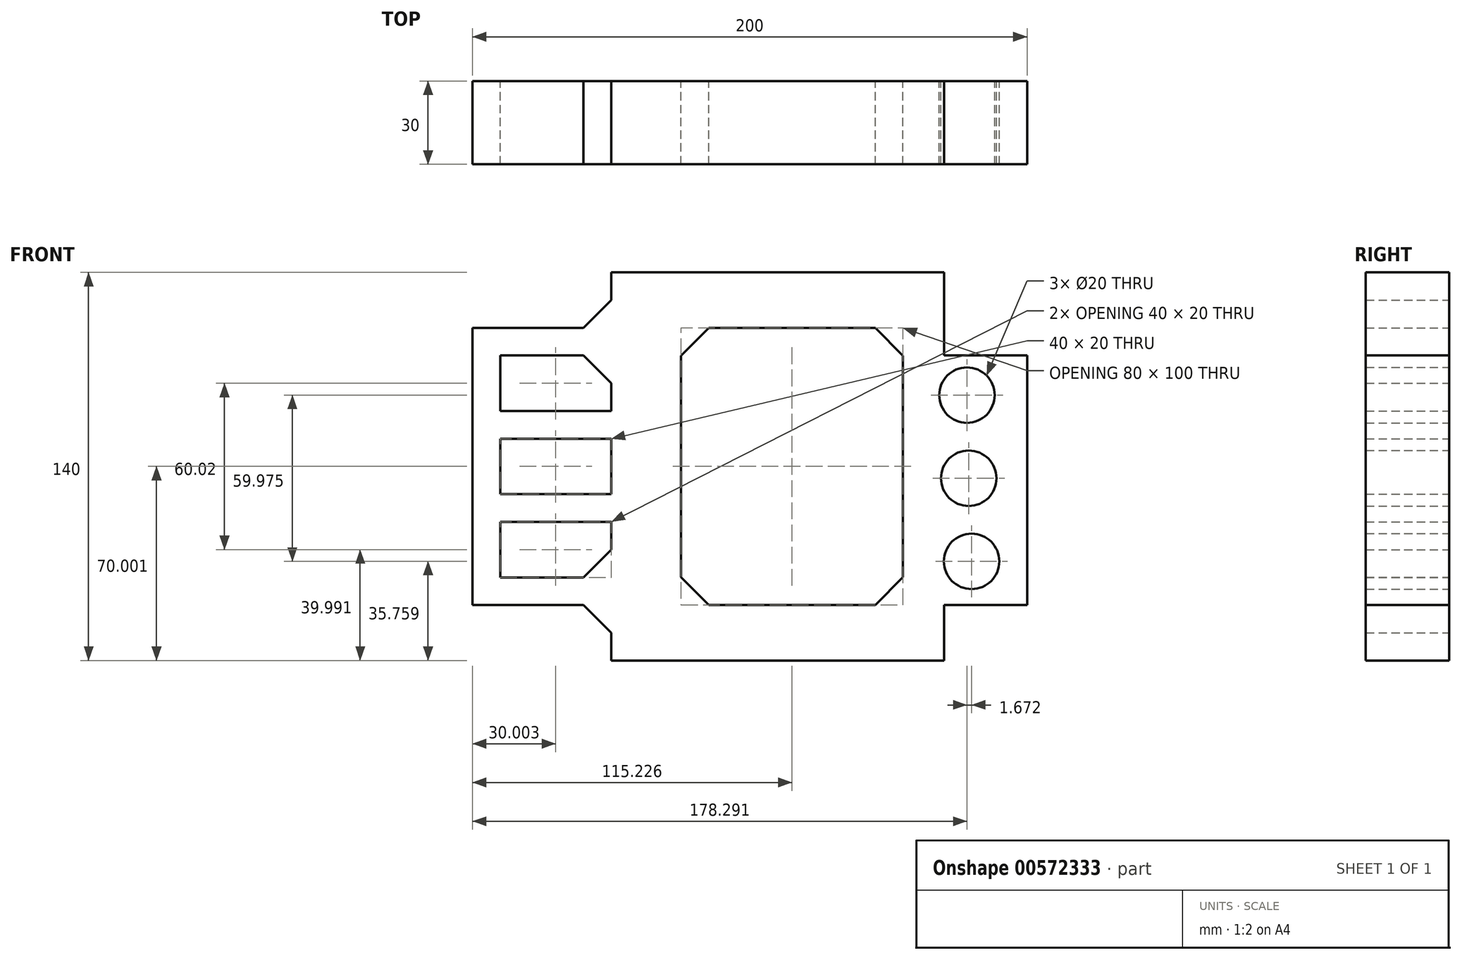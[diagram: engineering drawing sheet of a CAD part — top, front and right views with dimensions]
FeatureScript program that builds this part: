
annotation { "Feature Type Name" : "Feature", "Feature Type Description" : "" }
export const myFeature = defineFeature(function(context is Context, id is Id, definition is map)
    precondition{}
    {
        {
            var Q0;
            Q0=qCreatedBy(makeId("Front.planeOp"),FACE);
            var sketch = newSketch(context, id + "F0", { "sketchPlane" : qUnion([Q0])});
            skLineSegment(sketch, "E0", {"start": v(-36.99, 82.4) * mm, "end": v(63.01, 82.4) * mm});
            skLineSegment(sketch, "E1", {"start": v(73.01, 72.4) * mm, "end": v(73.01, 62.5) * mm});
            skLineSegment(sketch, "E2", {"start": v(83.01, 52.5) * mm, "end": v(93.01, 52.5) * mm});
            skLineSegment(sketch, "E3", {"start": v(103.01, 42.5) * mm, "end": v(103.01, -27.6) * mm});
            skLineSegment(sketch, "E4", {"start": v(93.01, -37.6) * mm, "end": v(83.01, -37.6) * mm});
            skLineSegment(sketch, "E5", {"start": v(73.01, -47.6) * mm, "end": v(73.01, -47.6) * mm});
            skLineSegment(sketch, "E6", {"start": v(63.01, -57.6) * mm, "end": v(-36.99, -57.6) * mm});
            skLineSegment(sketch, "E7", {"start": v(-46.99, -47.6) * mm, "end": v(-46.99, -47.6) * mm});
            skLineSegment(sketch, "E8", {"start": v(-56.99, -37.6) * mm, "end": v(-86.99, -37.6) * mm});
            skLineSegment(sketch, "E9", {"start": v(-96.99, -27.6) * mm, "end": v(-96.99, 52.4) * mm});
            skLineSegment(sketch, "E10", {"start": v(-86.99, 62.4) * mm, "end": v(-56.99, 62.4) * mm});
            skLineSegment(sketch, "E11", {"start": v(-46.99, 72.4) * mm, "end": v(-46.99, 72.4) * mm});
            skLineSegment(sketch, "E12", {"start": v(-11.76, 62.4) * mm, "end": v(48.24, 62.4) * mm});
            skLineSegment(sketch, "E13", {"start": v(58.24, 52.4) * mm, "end": v(58.24, 37.4) * mm});
            skLineSegment(sketch, "E14", {"start": v(48.24, -37.6) * mm, "end": v(-11.76, -37.6) * mm});
            skLineSegment(sketch, "E15", {"start": v(-21.76, -27.6) * mm, "end": v(-21.76, 12.4) * mm});
            skLineSegment(sketch, "E16.trimOffspring", {"start": v(-21.76, 37.4) * mm, "end": v(-21.76, 52.4) * mm});
            skLineSegment(sketch, "E17.trimOffspring", {"start": v(58.24, 12.4) * mm, "end": v(58.24, -27.6) * mm});
            skCircle(sketch, "E18", {"center": v(81.3, 38.13) * mm, "radius": 10 * mm});
            skCircle(sketch, "E19", {"center": v(82.97, -21.84) * mm, "radius": 10 * mm});
            skCircle(sketch, "E20", {"center": v(81.94, 8.14) * mm, "radius": 10 * mm});
            skLineSegment(sketch, "E21", {"start": v(-86.99, 52.41) * mm, "end": v(-86.99, 32.41) * mm});
            skLineSegment(sketch, "E22", {"start": v(-86.99, -27.6) * mm, "end": v(-56.99, -27.6) * mm});
            skLineSegment(sketch, "E23", {"start": v(-46.99, -17.6) * mm, "end": v(-46.99, -7.6) * mm});
            skLineSegment(sketch, "E24", {"start": v(-56.99, 52.41) * mm, "end": v(-86.99, 52.41) * mm});
            skLineSegment(sketch, "E25", {"start": v(-86.99, 32.41) * mm, "end": v(-46.99, 32.41) * mm});
            skLineSegment(sketch, "E26", {"start": v(-46.99, 22.4) * mm, "end": v(-86.99, 22.4) * mm});
            skLineSegment(sketch, "E27", {"start": v(-86.99, 2.4) * mm, "end": v(-46.99, 2.4) * mm});
            skLineSegment(sketch, "E28", {"start": v(-46.99, -7.6) * mm, "end": v(-86.99, -7.6) * mm});
            skLineSegment(sketch, "E29.trimOffspring", {"start": v(-46.99, 2.4) * mm, "end": v(-46.99, 22.4) * mm});
            skLineSegment(sketch, "E30.trimOffspring", {"start": v(-86.99, -7.6) * mm, "end": v(-86.99, -27.6) * mm});
            skLineSegment(sketch, "E31.trimOffspring", {"start": v(-86.99, 22.4) * mm, "end": v(-86.99, 2.4) * mm});
            skLineSegment(sketch, "E32.trimOffspring", {"start": v(-46.99, 32.41) * mm, "end": v(-46.99, 42.41) * mm});
            skPoint(sketch, "E33.visualSharp", {"position": v(73.01, 52.5) * mm});
            skPoint(sketch, "E34.visualSharp", {"position": v(-46.99, 62.4) * mm});
            skPoint(sketch, "E35.visualSharp", {"position": v(73.01, -37.6) * mm});
            skPoint(sketch, "E36.visualSharp", {"position": v(-46.99, -37.6) * mm});
            skPoint(sketch, "E37.visualSharp", {"position": v(-96.99, 62.4) * mm});
            skPoint(sketch, "E38.visualSharp", {"position": v(73.01, 82.4) * mm});
            skPoint(sketch, "E39.visualSharp", {"position": v(-46.99, 82.4) * mm});
            skPoint(sketch, "E40.visualSharp", {"position": v(103.01, 52.5) * mm});
            skPoint(sketch, "E41.visualSharp", {"position": v(103.01, -37.6) * mm});
            skPoint(sketch, "E42.visualSharp", {"position": v(73.01, -57.6) * mm});
            skPoint(sketch, "E43.visualSharp", {"position": v(-46.99, -57.6) * mm});
            skPoint(sketch, "E44.visualSharp", {"position": v(-96.99, -37.6) * mm});
            skPoint(sketch, "E45.visualSharp", {"position": v(-46.99, 52.41) * mm});
            skPoint(sketch, "E46.visualSharp", {"position": v(-46.99, -27.6) * mm});
            skPoint(sketch, "E47.visualSharp", {"position": v(58.24, 62.4) * mm});
            skPoint(sketch, "E48.visualSharp", {"position": v(-21.76, 62.4) * mm});
            skPoint(sketch, "E49.visualSharp", {"position": v(-21.76, -37.6) * mm});
            skPoint(sketch, "E50.visualSharp", {"position": v(58.24, -37.6) * mm});
            skLineSegment(sketch, "E51", {"start": v(-36.99, 82.4) * mm, "end": v(-46.99, 82.4) * mm});
            skLineSegment(sketch, "E52", {"start": v(-46.99, 82.4) * mm, "end": v(-46.99, 72.4) * mm});
            skLineSegment(sketch, "E53", {"start": v(63.01, 82.4) * mm, "end": v(73.01, 82.4) * mm});
            skLineSegment(sketch, "E54", {"start": v(73.01, 72.4) * mm, "end": v(73.01, 82.4) * mm});
            skLineSegment(sketch, "E55", {"start": v(73.01, 52.5) * mm, "end": v(73.01, 62.5) * mm});
            skLineSegment(sketch, "E56", {"start": v(73.01, 52.5) * mm, "end": v(83.01, 52.5) * mm});
            skLineSegment(sketch, "E57", {"start": v(93.01, 52.5) * mm, "end": v(103.01, 52.5) * mm});
            skLineSegment(sketch, "E58", {"start": v(103.01, 42.5) * mm, "end": v(103.01, 52.5) * mm});
            skLineSegment(sketch, "E59", {"start": v(-96.99, 62.4) * mm, "end": v(-86.99, 62.4) * mm});
            skLineSegment(sketch, "E60", {"start": v(-96.99, 52.4) * mm, "end": v(-96.99, 62.4) * mm});
            skLineSegment(sketch, "E61", {"start": v(-96.99, -27.6) * mm, "end": v(-96.99, -37.6) * mm});
            skLineSegment(sketch, "E62", {"start": v(-86.99, -37.6) * mm, "end": v(-96.99, -37.6) * mm});
            skLineSegment(sketch, "E63", {"start": v(-46.99, -47.6) * mm, "end": v(-46.99, -57.6) * mm});
            skLineSegment(sketch, "E64", {"start": v(-36.99, -57.6) * mm, "end": v(-46.99, -57.6) * mm});
            skLineSegment(sketch, "E65", {"start": v(73.01, -47.6) * mm, "end": v(73.01, -57.6) * mm});
            skLineSegment(sketch, "E66", {"start": v(63.01, -57.6) * mm, "end": v(73.01, -57.6) * mm});
            skLineSegment(sketch, "E67", {"start": v(93.01, -37.6) * mm, "end": v(103.01, -37.6) * mm});
            skLineSegment(sketch, "E68", {"start": v(103.01, -27.6) * mm, "end": v(103.01, -37.6) * mm});
            skLineSegment(sketch, "E69", {"start": v(-11.76, 62.4) * mm, "end": v(-21.76, 52.4) * mm});
            skLineSegment(sketch, "E70", {"start": v(48.24, 62.4) * mm, "end": v(58.24, 52.4) * mm});
            skLineSegment(sketch, "E71", {"start": v(58.24, 37.4) * mm, "end": v(58.24, 12.4) * mm});
            skLineSegment(sketch, "E72", {"start": v(58.24, -27.6) * mm, "end": v(48.24, -37.6) * mm});
            skLineSegment(sketch, "E73", {"start": v(-11.76, -37.6) * mm, "end": v(-21.76, -27.6) * mm});
            skLineSegment(sketch, "E74", {"start": v(-21.76, 12.4) * mm, "end": v(-21.76, 37.4) * mm});
            skLineSegment(sketch, "E75", {"start": v(-56.99, 52.41) * mm, "end": v(-46.99, 42.41) * mm});
            skLineSegment(sketch, "E76", {"start": v(-46.99, -17.6) * mm, "end": v(-56.99, -27.6) * mm});
            skLineSegment(sketch, "E77", {"start": v(73.01, -37.6) * mm, "end": v(73.01, -47.6) * mm});
            skLineSegment(sketch, "E78", {"start": v(73.01, -37.6) * mm, "end": v(83.01, -37.6) * mm});
            skLineSegment(sketch, "E79", {"start": v(-56.99, -37.6) * mm, "end": v(-46.99, -47.6) * mm});
            skLineSegment(sketch, "E80", {"start": v(-56.99, 62.4) * mm, "end": v(-46.99, 72.4) * mm});
            skSolve(sketch);
        }
        {
            var Q0;
            Q0 = qSketchRegion(id + "F0", true);
            extrude(context, id + "F1", {"entities" : qUnion([Q0]), "depth" : 30 * mm, "offsetDistance" : 25 * mm});
        }
    });
